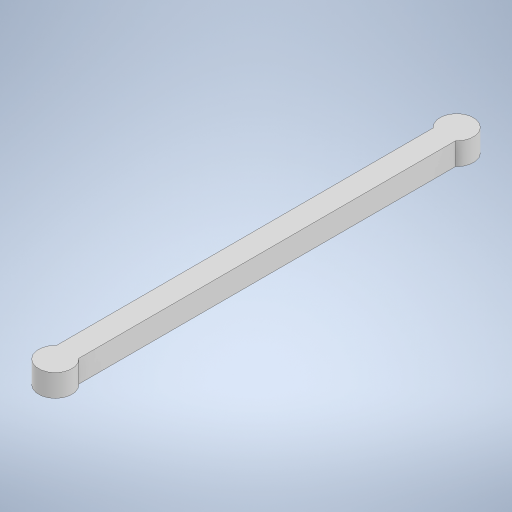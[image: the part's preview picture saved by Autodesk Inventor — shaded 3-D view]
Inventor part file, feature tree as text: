
AUTODESK INVENTOR PART (.ipt)
format: ipt  version: 2024.3 (Build 283343000, 343)  size: 236,032 bytes
history: native  units: mm
features: other x1, extrude x1, sketch x1
ambient origin geometry x8: Origin, YZ Plane, XZ Plane, XY Plane, X Axis, Y Axis, Z Axis, Center Point
bodies: Body1 (feature_tree)
feature tree (3):
  other  "ソリッド1"
  extrude  "押し出し1"  Depth=180.0mm
  sketch  "スケッチ1"
